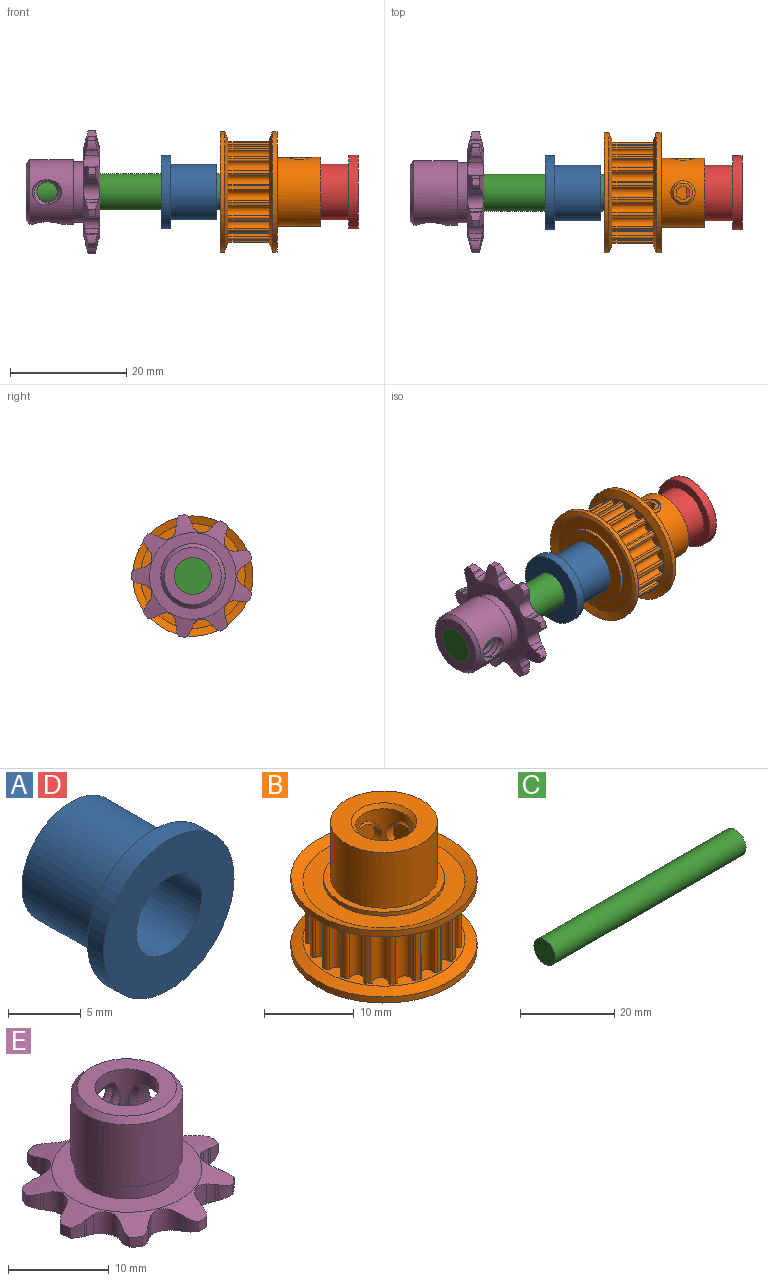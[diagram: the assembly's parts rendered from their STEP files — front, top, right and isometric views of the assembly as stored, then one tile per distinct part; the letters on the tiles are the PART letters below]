
ASSEMBLY  parts=5 mates=4
PART A: 6 faces, bbox 12.7x9.5x12.7 mm
  f0: cylinder r=6.35mm len=12.7mm, axis (0,-1,0), area 63.3mm2, adj f4,f5
  f1: cylinder r=3.19mm len=9.53mm, axis (0,-1,0), area 190.8mm2, adj f3,f4
  f2: cylinder r=4.79mm len=9.58mm, axis (0,-1,0), area 238.8mm2, adj f3,f5
  f3: plane 9.58x9.58mm, normal (0,1,0), area 40.1mm2, adj f1,f2
  f4: plane 12.7x12.7mm, normal (0,-1,0), area 94.8mm2, adj f0,f1
  f5: plane 12.7x12.7mm, normal (0,1,0), area 54.7mm2, adj f0,f2
PART B: 121 faces, bbox 20.7x20.7x17.3 mm
  f0: plane 11.89x11.89mm, normal (0,0,1), area 69.1mm2, adj f1,f6
  f1: cone r=3.41mm half-angle=45deg, axis (0,0,1), area 14.4mm2, adj f0,f2
  f2: cylinder r=3.17mm len=16.39mm, axis (0,0,-1), area 298mm2, adj f1,f4,f31,f99
  f3: cylinder r=2.08mm len=4.17mm, axis (0,-1,0), area 3mm2, adj f5,f6
  f4: cylinder r=2.08mm len=4.17mm, axis (0,-1,0), area 10.4mm2, adj f2,f119
  f5: cone r=1.87mm half-angle=45deg, axis (0,-1,0), area 6.9mm2, adj f3,f111
  f6: cylinder r=5.94mm len=11.89mm, axis (0,0,-1), area 253.9mm2, adj f0,f3,f7,f98
  f7: plane 13.46x13.46mm, normal (0,0,1), area 31.4mm2, adj f6,f8
  f8: cylinder r=6.73mm len=13.46mm, axis (0,0,-1), area 22.6mm2, adj f7,f9
  f9: plane 18.03x18.03mm, normal (0,0,1), area 113.1mm2, adj f8,f10
  f10: cone r=9.68mm half-angle=68.2deg, axis (0,0,1), area 87.4mm2, adj f9,f11
  f11: cylinder r=10.35mm len=20.7mm, axis (0,0,-1), area 52.9mm2, adj f10,f12
  f12: cone r=9.68mm half-angle=68.2deg, axis (0,0,1), area 87.4mm2, adj f11,f13
  f13: plane 18.03x18.03mm, normal (0,0,-1), area 55.8mm2, adj f12,f14,f15,f16,f17,f18,f19,f20
  f14: cylinder r=8.69mm len=7.11mm, axis (0,0,-1), area 4.1mm2, adj f13,f24,f32,f97
  f15: cylinder r=8.69mm len=7.11mm, axis (0,0,-1), area 4.1mm2, adj f13,f24,f94,f95
  f16: cylinder r=8.69mm len=7.11mm, axis (0,0,-1), area 4.1mm2, adj f13,f24,f91,f92
  f17: cylinder r=8.69mm len=7.11mm, axis (0,0,-1), area 4.1mm2, adj f13,f24,f88,f89
  f18: cylinder r=8.69mm len=7.11mm, axis (0,0,-1), area 4.1mm2, adj f13,f24,f85,f86
  f19: cylinder r=8.69mm len=7.11mm, axis (0,0,-1), area 4.1mm2, adj f13,f24,f82,f83
  f20: cylinder r=8.69mm len=7.11mm, axis (0,0,-1), area 4.1mm2, adj f13,f24,f79,f80
  f21: cylinder r=8.69mm len=7.11mm, axis (0,0,-1), area 4.1mm2, adj f13,f24,f76,f77
  f22: cylinder r=8.69mm len=7.11mm, axis (0,0,-1), area 4.1mm2, adj f13,f24,f73,f74
  f23: cylinder r=8.69mm len=7.11mm, axis (0,0,-1), area 4.1mm2, adj f13,f24,f49,f71
  f24: plane 18.03x18.03mm, normal (0,0,1), area 55.8mm2, adj f14,f15,f16,f17,f18,f19,f20,f21
  f25: cone r=9.68mm half-angle=68.2deg, axis (0,0,-1), area 87.4mm2, adj f24,f26
  f26: cylinder r=10.35mm len=20.7mm, axis (0,0,-1), area 52.9mm2, adj f25,f27
  f27: cone r=9.68mm half-angle=68.2deg, axis (0,0,-1), area 87.4mm2, adj f26,f28
  f28: plane 18.03x18.03mm, normal (0,0,-1), area 113.1mm2, adj f27,f29
  f29: cylinder r=6.73mm len=13.46mm, axis (0,0,-1), area 22.6mm2, adj f28,f30
  f30: plane 13.46x13.46mm, normal (0,0,-1), area 100.5mm2, adj f29,f31
  f31: cone r=3.41mm half-angle=45deg, axis (0,0,-1), area 14.4mm2, adj f2,f30
  f32: cylinder r=0.25mm len=7.11mm, axis (0,0,1), area 3.3mm2, adj f13,f14,f24,f33
  f33: cylinder r=0.86mm len=7.11mm, axis (0,0,1), area 20.7mm2, adj f13,f24,f32,f34
  f34: cylinder r=0.25mm len=7.11mm, axis (0,0,1), area 3.3mm2, adj f13,f24,f33,f43
  f35: cylinder r=8.69mm len=7.11mm, axis (0,0,-1), area 4.1mm2, adj f13,f24,f44,f47
  f36: cylinder r=8.69mm len=7.11mm, axis (0,0,-1), area 4.1mm2, adj f13,f24,f46,f50
  f37: cylinder r=8.69mm len=7.11mm, axis (0,0,-1), area 4.1mm2, adj f13,f24,f52,f53
  f38: cylinder r=8.69mm len=7.11mm, axis (0,0,-1), area 4.1mm2, adj f13,f24,f55,f56
  f39: cylinder r=8.69mm len=7.11mm, axis (0,0,-1), area 4.1mm2, adj f13,f24,f58,f59
  f40: cylinder r=8.69mm len=7.11mm, axis (0,0,-1), area 4.1mm2, adj f13,f24,f61,f62
  f41: cylinder r=8.69mm len=7.11mm, axis (0,0,-1), area 4.1mm2, adj f13,f24,f64,f65
  f42: cylinder r=8.69mm len=7.11mm, axis (0,0,-1), area 4.1mm2, adj f13,f24,f67,f68
  f43: cylinder r=8.69mm len=7.11mm, axis (0,0,-1), area 4.1mm2, adj f13,f24,f34,f70
  f44: cylinder r=0.25mm len=7.11mm, axis (0,0,1), area 3.3mm2, adj f13,f24,f35,f45
  f45: cylinder r=0.86mm len=7.11mm, axis (0,0,1), area 20.7mm2, adj f13,f24,f44,f46
  f46: cylinder r=0.25mm len=7.11mm, axis (0,0,1), area 3.3mm2, adj f13,f24,f36,f45
  f47: cylinder r=0.25mm len=7.11mm, axis (0,0,1), area 3.3mm2, adj f13,f24,f35,f48
  f48: cylinder r=0.86mm len=7.11mm, axis (0,0,1), area 20.7mm2, adj f13,f24,f47,f49
  f49: cylinder r=0.25mm len=7.11mm, axis (0,0,1), area 3.3mm2, adj f13,f23,f24,f48
  f50: cylinder r=0.25mm len=7.11mm, axis (0,0,1), area 3.3mm2, adj f13,f24,f36,f51
  f51: cylinder r=0.86mm len=7.11mm, axis (0,0,1), area 20.7mm2, adj f13,f24,f50,f52
  f52: cylinder r=0.25mm len=7.11mm, axis (0,0,1), area 3.3mm2, adj f13,f24,f37,f51
  f53: cylinder r=0.25mm len=7.11mm, axis (0,0,1), area 3.3mm2, adj f13,f24,f37,f54
  f54: cylinder r=0.86mm len=7.11mm, axis (0,0,1), area 20.7mm2, adj f13,f24,f53,f55
  f55: cylinder r=0.25mm len=7.11mm, axis (0,0,1), area 3.3mm2, adj f13,f24,f38,f54
  f56: cylinder r=0.25mm len=7.11mm, axis (0,0,1), area 3.3mm2, adj f13,f24,f38,f57
  f57: cylinder r=0.86mm len=7.11mm, axis (0,0,1), area 20.7mm2, adj f13,f24,f56,f58
  f58: cylinder r=0.25mm len=7.11mm, axis (0,0,1), area 3.3mm2, adj f13,f24,f39,f57
  f59: cylinder r=0.25mm len=7.11mm, axis (0,0,1), area 3.3mm2, adj f13,f24,f39,f60
  f60: cylinder r=0.86mm len=7.11mm, axis (0,0,1), area 20.7mm2, adj f13,f24,f59,f61
  f61: cylinder r=0.25mm len=7.11mm, axis (0,0,1), area 3.3mm2, adj f13,f24,f40,f60
  f62: cylinder r=0.25mm len=7.11mm, axis (0,0,1), area 3.3mm2, adj f13,f24,f40,f63
  f63: cylinder r=0.86mm len=7.11mm, axis (0,0,1), area 20.7mm2, adj f13,f24,f62,f64
  f64: cylinder r=0.25mm len=7.11mm, axis (0,0,1), area 3.3mm2, adj f13,f24,f41,f63
  f65: cylinder r=0.25mm len=7.11mm, axis (0,0,1), area 3.3mm2, adj f13,f24,f41,f66
  f66: cylinder r=0.86mm len=7.11mm, axis (0,0,1), area 20.7mm2, adj f13,f24,f65,f67
  f67: cylinder r=0.25mm len=7.11mm, axis (0,0,1), area 3.3mm2, adj f13,f24,f42,f66
  f68: cylinder r=0.25mm len=7.11mm, axis (0,0,1), area 3.3mm2, adj f13,f24,f42,f69
  f69: cylinder r=0.86mm len=7.11mm, axis (0,0,1), area 20.7mm2, adj f13,f24,f68,f70
  f70: cylinder r=0.25mm len=7.11mm, axis (0,0,1), area 3.3mm2, adj f13,f24,f43,f69
  f71: cylinder r=0.25mm len=7.11mm, axis (0,0,1), area 3.3mm2, adj f13,f23,f24,f72
  f72: cylinder r=0.86mm len=7.11mm, axis (0,0,1), area 20.7mm2, adj f13,f24,f71,f73
  f73: cylinder r=0.25mm len=7.11mm, axis (0,0,1), area 3.3mm2, adj f13,f22,f24,f72
  f74: cylinder r=0.25mm len=7.11mm, axis (0,0,1), area 3.3mm2, adj f13,f22,f24,f75
  f75: cylinder r=0.86mm len=7.11mm, axis (0,0,1), area 20.7mm2, adj f13,f24,f74,f76
  f76: cylinder r=0.25mm len=7.11mm, axis (0,0,1), area 3.3mm2, adj f13,f21,f24,f75
  f77: cylinder r=0.25mm len=7.11mm, axis (0,0,1), area 3.3mm2, adj f13,f21,f24,f78
  f78: cylinder r=0.86mm len=7.11mm, axis (0,0,1), area 20.7mm2, adj f13,f24,f77,f79
  f79: cylinder r=0.25mm len=7.11mm, axis (0,0,1), area 3.3mm2, adj f13,f20,f24,f78
  f80: cylinder r=0.25mm len=7.11mm, axis (0,0,1), area 3.3mm2, adj f13,f20,f24,f81
  f81: cylinder r=0.86mm len=7.11mm, axis (0,0,1), area 20.7mm2, adj f13,f24,f80,f82
  f82: cylinder r=0.25mm len=7.11mm, axis (0,0,1), area 3.3mm2, adj f13,f19,f24,f81
  f83: cylinder r=0.25mm len=7.11mm, axis (0,0,1), area 3.3mm2, adj f13,f19,f24,f84
  f84: cylinder r=0.86mm len=7.11mm, axis (0,0,1), area 20.7mm2, adj f13,f24,f83,f85
  f85: cylinder r=0.25mm len=7.11mm, axis (0,0,1), area 3.3mm2, adj f13,f18,f24,f84
  f86: cylinder r=0.25mm len=7.11mm, axis (0,0,1), area 3.3mm2, adj f13,f18,f24,f87
  f87: cylinder r=0.86mm len=7.11mm, axis (0,0,1), area 20.7mm2, adj f13,f24,f86,f88
  f88: cylinder r=0.25mm len=7.11mm, axis (0,0,1), area 3.3mm2, adj f13,f17,f24,f87
  f89: cylinder r=0.25mm len=7.11mm, axis (0,0,1), area 3.3mm2, adj f13,f17,f24,f90
  f90: cylinder r=0.86mm len=7.11mm, axis (0,0,1), area 20.7mm2, adj f13,f24,f89,f91
  f91: cylinder r=0.25mm len=7.11mm, axis (0,0,1), area 3.3mm2, adj f13,f16,f24,f90
  f92: cylinder r=0.25mm len=7.11mm, axis (0,0,1), area 3.3mm2, adj f13,f16,f24,f93
  f93: cylinder r=0.86mm len=7.11mm, axis (0,0,1), area 20.7mm2, adj f13,f24,f92,f94
  f94: cylinder r=0.25mm len=7.11mm, axis (0,0,1), area 3.3mm2, adj f13,f15,f24,f93
  f95: cylinder r=0.25mm len=7.11mm, axis (0,0,1), area 3.3mm2, adj f13,f15,f24,f96
  f96: cylinder r=0.86mm len=7.11mm, axis (0,0,1), area 20.7mm2, adj f13,f24,f95,f97
  f97: cylinder r=0.25mm len=7.11mm, axis (0,0,1), area 3.3mm2, adj f13,f14,f24,f96
  f98: cylinder r=2.08mm len=4.17mm, axis (-1,0,0), area 3mm2, adj f6,f100
  f99: cylinder r=2.08mm len=4.17mm, axis (-1,0,0), area 10.4mm2, adj f2,f101
  f100: cone r=1.87mm half-angle=45deg, axis (-1,0,0), area 6.9mm2, adj f98,f103
  f101: cone r=1.87mm half-angle=45deg, axis (1,0,0), area 6.9mm2, adj f99,f102
  f102: plane 3.33x3.33mm, normal (-1,0,0), area 8.7mm2, adj f101
  f103: plane 3.33x3.33mm, normal (1,0,0), area 5mm2, adj f100,f104,f105,f106,f107,f108,f109
  f104: plane 2.08x1.04mm, normal (0,-0.87,0.5), area 2.5mm2, adj f103,f105,f109,f110
  f105: plane 2.08x1.2mm, normal (0,0,1), area 2.5mm2, adj f103,f104,f106,f110
  f106: plane 2.08x1.04mm, normal (0,0.87,0.5), area 2.5mm2, adj f103,f105,f107,f110
  f107: plane 2.08x1.04mm, normal (0,0.87,-0.5), area 2.5mm2, adj f103,f106,f108,f110
  f108: plane 2.08x1.2mm, normal (0,0,-1), area 2.5mm2, adj f103,f107,f109,f110
  f109: plane 2.08x1.04mm, normal (0,-0.87,-0.5), area 2.5mm2, adj f103,f104,f108,f110
  f110: plane 2.41x2.08mm, normal (1,0,0), area 3.8mm2, adj f104,f105,f106,f107,f108,f109
  f111: plane 3.33x3.33mm, normal (0,1,0), area 5mm2, adj f5,f112,f113,f114,f115,f116,f117
  f112: plane 2.08x1.04mm, normal (0.87,0,0.5), area 2.5mm2, adj f111,f113,f117,f118
  f113: plane 2.08x1.2mm, normal (0,0,1), area 2.5mm2, adj f111,f112,f114,f118
  f114: plane 2.08x1.04mm, normal (-0.87,0,0.5), area 2.5mm2, adj f111,f113,f115,f118
  f115: plane 2.08x1.04mm, normal (-0.87,0,-0.5), area 2.5mm2, adj f111,f114,f116,f118
  f116: plane 2.08x1.2mm, normal (0,0,-1), area 2.5mm2, adj f111,f115,f117,f118
  f117: plane 2.08x1.04mm, normal (0.87,0,-0.5), area 2.5mm2, adj f111,f112,f116,f118
  f118: plane 2.41x2.08mm, normal (0,1,0), area 3.8mm2, adj f112,f113,f114,f115,f116,f117
  f119: cone r=1.87mm half-angle=45deg, axis (0,1,0), area 6.9mm2, adj f4,f120
  f120: plane 3.33x3.33mm, normal (0,-1,0), area 8.7mm2, adj f119
PART C: 3 faces, bbox 57.2x6.4x6.4 mm
  f0: cylinder r=3.17mm len=57.15mm, axis (-1,0,0), area 1140.1mm2, adj f1,f2
  f1: plane 6.35x6.35mm, normal (1,0,0), area 31.7mm2, adj f0
  f2: plane 6.35x6.35mm, normal (-1,0,0), area 31.7mm2, adj f0
PART D: same geometry as A
PART E: 104 faces, bbox 21.3x21.3x12.7 mm
  f0: cone r=2.53mm half-angle=45deg, axis (1,0,0), area 5.2mm2, adj f1,f100,f101,f102,f103
  f1: cylinder r=1.75mm len=3.5mm, axis (1,0,0), area 3mm2, adj f0,f2,f100,f103
  f2: cylinder r=3.17mm len=12.7mm, axis (0,0,-1), area 224.8mm2, adj f1,f3,f4,f7,f8,f9,f10,f11
  f3: cylinder r=1.75mm len=1.44mm, axis (0,1,0), area 0mm2, adj f2,f11
  f4: cylinder r=1.75mm len=3.5mm, axis (0,1,0), area 3mm2, adj f2,f5,f9,f11
  f5: cone r=2.53mm half-angle=45deg, axis (0,1,0), area 5.2mm2, adj f4,f6,f9,f11,f102
  f6: cylinder r=2.41mm len=0.66mm, axis (0,1,0), area 0mm2, adj f5,f11,f102
  f7: bspline ~3.65x1.27mm, area 0mm2, adj f2,f8
  f8: cylinder r=2.41mm len=3.57mm, axis (0,1,0), area 0.5mm2, adj f2,f7,f9
  f9: bspline ~4.83x4.83mm, area 21.5mm2, adj f2,f4,f5,f8,f10,f102
  f10: cylinder r=2.41mm len=4.83mm, axis (0,1,0), area 4.2mm2, adj f2,f9,f11,f102
  f11: bspline ~4.82x4.82mm, area 21.8mm2, adj f2,f3,f4,f5,f6,f10,f102
  f12: cylinder r=2.41mm len=1.46mm, axis (1,0,0), area 0mm2, adj f2,f13
  f13: bspline ~1.77x0.52mm, area 0mm2, adj f2,f12
  f14: bspline ~1.77x0.52mm, area 0mm2, adj f2,f15
  f15: cylinder r=2.41mm len=1.46mm, axis (0,1,0), area 0.1mm2, adj f2,f14,f16
  f16: bspline ~3.65x1.26mm, area 0.7mm2, adj f2,f15,f17
  f17: cylinder r=2.41mm len=3.57mm, axis (1,0,0), area 0.5mm2, adj f2,f16,f103
  f18: plane 9.84x9.84mm, normal (0,0,1), area 44.4mm2, adj f2,f19
  f19: cone r=4.92mm half-angle=45deg, axis (0,0,-1), area 29.6mm2, adj f18,f102
  f20: cylinder r=2.41mm len=4.83mm, axis (1,0,0), area 4.2mm2, adj f2,f100,f102,f103
  f21: cylinder r=1.75mm len=1.44mm, axis (1,0,0), area 0mm2, adj f2,f100
  f22: plane 14.91x14.91mm, normal (0,0,-1), area 142.8mm2, adj f2,f23
  f23: cone r=7.45mm half-angle=76deg, axis (0,0,1), area 84mm2, adj f22,f24,f29,f30,f31,f32,f33,f34
  f24: cylinder r=1.7mm len=2.5mm, axis (0,0,1), area 6.9mm2, adj f23,f25,f29,f99
  f25: cone r=10.63mm half-angle=76deg, axis (0,0,-1), area 84mm2, adj f24,f26,f29,f30,f31,f32,f33,f34
  f26: plane 14.91x14.91mm, normal (0,0,1), area 90.6mm2, adj f25,f27
  f27: cylinder r=5.17mm len=10.33mm, axis (0,0,-1), area 56.7mm2, adj f26,f28
  f28: plane 11.11x11.11mm, normal (0,0,-1), area 13.1mm2, adj f27,f102
  f29: cylinder r=4.34mm len=2.39mm, axis (0,0,1), area 2mm2, adj f23,f24,f25,f30
  f30: plane 1.99x0.2mm, normal (0.64,-0.77,0), area 0.5mm2, adj f23,f25,f29,f31
  f31: cylinder r=2.8mm len=1.87mm, axis (0,0,1), area 2.4mm2, adj f23,f25,f30,f32
  f32: cylinder r=10.63mm len=1.21mm, axis (0,0,-1), area 1.5mm2, adj f23,f25,f31,f33
  f33: cylinder r=2.8mm len=1.87mm, axis (0,0,1), area 2.4mm2, adj f23,f25,f32,f34
  f34: plane 1.99x0.24mm, normal (-0.34,0.94,0), area 0.5mm2, adj f23,f25,f33,f35
  f35: cylinder r=4.34mm len=2.39mm, axis (0,0,1), area 2mm2, adj f23,f25,f34,f36
  f36: cylinder r=1.7mm len=2.39mm, axis (0,0,1), area 6.9mm2, adj f23,f25,f35,f37
  f37: cylinder r=4.34mm len=2.39mm, axis (0,0,1), area 2mm2, adj f23,f25,f36,f38
  f38: plane 1.99x0.25mm, normal (0.98,-0.18,0), area 0.5mm2, adj f23,f25,f37,f39
  f39: cylinder r=2.8mm len=1.87mm, axis (0,0,1), area 2.4mm2, adj f23,f25,f38,f40
  f40: cylinder r=10.63mm len=1.21mm, axis (0,0,-1), area 1.5mm2, adj f23,f25,f39,f41
  f41: cylinder r=2.8mm len=1.87mm, axis (0,0,1), area 2.4mm2, adj f23,f25,f40,f42
  f42: plane 1.99x0.22mm, normal (-0.87,0.5,0), area 0.5mm2, adj f23,f25,f41,f43
  f43: cylinder r=4.34mm len=2.39mm, axis (0,0,1), area 2mm2, adj f23,f25,f42,f44
  f44: cylinder r=1.7mm len=2.54mm, axis (0,0,1), area 6.9mm2, adj f23,f25,f43,f45
  f45: cylinder r=4.34mm len=2.39mm, axis (0,0,1), area 2mm2, adj f23,f25,f44,f46
  f46: plane 1.99x0.22mm, normal (0.87,0.5,0), area 0.5mm2, adj f23,f25,f45,f47
  f47: cylinder r=2.8mm len=1.87mm, axis (0,0,1), area 2.4mm2, adj f23,f25,f46,f48
  f48: cylinder r=10.63mm len=1.21mm, axis (0,0,-1), area 1.5mm2, adj f23,f25,f47,f49
  f49: cylinder r=2.8mm len=1.87mm, axis (0,0,1), area 2.4mm2, adj f23,f25,f48,f50
  f50: plane 1.99x0.25mm, normal (-0.98,-0.18,0), area 0.5mm2, adj f23,f25,f49,f51
  f51: cylinder r=4.34mm len=2.39mm, axis (0,0,1), area 2mm2, adj f23,f25,f50,f52
  f52: cylinder r=1.7mm len=2.39mm, axis (0,0,1), area 6.9mm2, adj f23,f25,f51,f53
  f53: cylinder r=4.34mm len=2.39mm, axis (0,0,1), area 2mm2, adj f23,f25,f52,f54
  f54: plane 1.99x0.24mm, normal (0.34,0.94,0), area 0.5mm2, adj f23,f25,f53,f55
  f55: cylinder r=2.8mm len=1.87mm, axis (0,0,1), area 2.4mm2, adj f23,f25,f54,f56
  f56: cylinder r=10.63mm len=1.21mm, axis (0,0,-1), area 1.5mm2, adj f23,f25,f55,f57
  f57: cylinder r=2.8mm len=1.87mm, axis (0,0,1), area 2.4mm2, adj f23,f25,f56,f58
  f58: plane 1.99x0.2mm, normal (-0.64,-0.77,0), area 0.5mm2, adj f23,f25,f57,f59
  f59: cylinder r=4.34mm len=2.39mm, axis (0,0,1), area 2mm2, adj f23,f25,f58,f60
  f60: cylinder r=1.7mm len=2.71mm, axis (0,0,1), area 7.3mm2, adj f23,f25,f59,f61
  f61: cylinder r=4.34mm len=2.39mm, axis (0,0,1), area 2mm2, adj f23,f25,f60,f62
  f62: plane 1.99x0.24mm, normal (-0.34,0.94,0), area 0.5mm2, adj f23,f25,f61,f63
  f63: cylinder r=2.8mm len=1.87mm, axis (0,0,1), area 2.4mm2, adj f23,f25,f62,f64
  f64: cylinder r=10.63mm len=1.23mm, axis (0,0,-1), area 1.5mm2, adj f23,f25,f63,f65
  f65: cylinder r=2.8mm len=1.87mm, axis (0,0,1), area 2.4mm2, adj f23,f25,f64,f66
  f66: plane 1.99x0.26mm, normal (0,-1,0), area 0.5mm2, adj f23,f25,f65,f67
  f67: cylinder r=4.34mm len=2.39mm, axis (0,0,1), area 2mm2, adj f23,f25,f66,f68
  f68: cylinder r=1.7mm len=2.59mm, axis (0,0,1), area 7.1mm2, adj f23,f25,f67,f69
  f69: cylinder r=4.34mm len=2.39mm, axis (0,0,1), area 2mm2, adj f23,f25,f68,f70
  f70: plane 1.99x0.22mm, normal (-0.87,0.5,0), area 0.5mm2, adj f23,f25,f69,f71
  f71: cylinder r=2.8mm len=1.87mm, axis (0,0,1), area 2.4mm2, adj f23,f25,f70,f72
  f72: cylinder r=10.63mm len=1.21mm, axis (0,0,-1), area 1.5mm2, adj f23,f25,f71,f73
  f73: cylinder r=2.8mm len=1.87mm, axis (0,0,1), area 2.4mm2, adj f23,f25,f72,f74
  f74: plane 1.99x0.2mm, normal (0.64,-0.76,0), area 0.5mm2, adj f23,f25,f73,f75
  f75: cylinder r=4.34mm len=2.39mm, axis (0,0,1), area 2mm2, adj f23,f25,f74,f76
  f76: cylinder r=1.7mm len=2.39mm, axis (0,0,1), area 6.9mm2, adj f23,f25,f75,f77
  f77: cylinder r=4.34mm len=2.39mm, axis (0,0,1), area 2mm2, adj f23,f25,f76,f78
  f78: plane 1.99x0.25mm, normal (-0.99,-0.17,0), area 0.5mm2, adj f23,f25,f77,f79
  f79: cylinder r=2.8mm len=1.87mm, axis (0,0,1), area 2.4mm2, adj f23,f25,f78,f80
  f80: cylinder r=10.63mm len=1.25mm, axis (0,0,-1), area 1.5mm2, adj f23,f25,f79,f81
  f81: cylinder r=2.8mm len=1.87mm, axis (0,0,1), area 2.4mm2, adj f23,f25,f80,f82
  f82: plane 1.99x0.25mm, normal (0.99,-0.17,0), area 0.5mm2, adj f23,f25,f81,f83
  f83: cylinder r=4.34mm len=2.39mm, axis (0,0,1), area 2mm2, adj f23,f25,f82,f84
  f84: cylinder r=1.7mm len=2.39mm, axis (0,0,1), area 6.9mm2, adj f23,f25,f83,f85
  f85: cylinder r=4.34mm len=2.39mm, axis (0,0,1), area 2mm2, adj f23,f25,f84,f86
  f86: plane 1.99x0.2mm, normal (-0.64,-0.76,0), area 0.5mm2, adj f23,f25,f85,f87
  f87: cylinder r=2.8mm len=1.87mm, axis (0,0,1), area 2.4mm2, adj f23,f25,f86,f88
  f88: cylinder r=10.63mm len=1.21mm, axis (0,0,-1), area 1.5mm2, adj f23,f25,f87,f89
  f89: cylinder r=2.8mm len=1.87mm, axis (0,0,1), area 2.4mm2, adj f23,f25,f88,f90
  f90: plane 1.99x0.22mm, normal (0.87,0.5,0), area 0.5mm2, adj f23,f25,f89,f91
  f91: cylinder r=4.34mm len=2.39mm, axis (0,0,1), area 2mm2, adj f23,f25,f90,f92
  f92: cylinder r=1.7mm len=2.39mm, axis (0,0,1), area 6.9mm2, adj f23,f25,f91,f93
  f93: cylinder r=4.34mm len=2.39mm, axis (0,0,1), area 2mm2, adj f23,f25,f92,f94
  f94: plane 1.99x0.26mm, normal (0,-1,0), area 0.5mm2, adj f23,f25,f93,f95
  f95: cylinder r=2.8mm len=1.87mm, axis (0,0,1), area 2.4mm2, adj f23,f25,f94,f96
  f96: cylinder r=10.63mm len=1.23mm, axis (0,0,-1), area 1.5mm2, adj f23,f25,f95,f97
  f97: cylinder r=2.8mm len=1.87mm, axis (0,0,1), area 2.4mm2, adj f23,f25,f96,f98
  f98: plane 1.99x0.24mm, normal (0.34,0.94,0), area 0.5mm2, adj f23,f25,f97,f99
  f99: cylinder r=4.34mm len=2.39mm, axis (0,0,1), area 2mm2, adj f23,f24,f25,f98
  f100: bspline ~4.82x4.82mm, area 21.9mm2, adj f0,f1,f2,f20,f21,f101,f102
  f101: cylinder r=2.41mm len=0.66mm, axis (1,0,0), area 0mm2, adj f0,f100,f102
  f102: cylinder r=5.56mm len=11.11mm, axis (0,0,-1), area 227.9mm2, adj f0,f5,f6,f9,f10,f11,f19,f20
  f103: bspline ~4.83x4.83mm, area 21.6mm2, adj f0,f1,f2,f17,f20,f102
PLACE A rot(axis=(-0.58,-0.58,-0.58),120deg) t=(98.58,138.17,34.25)mm
PLACE B rot(axis=(0.58,0.58,0.58),120deg) t=(118.49,138.17,34.25)mm
PLACE C rot(axis=(0,1,0),180deg) t=(157.82,-50.53,49.28)mm
PLACE D rot(axis=(0,0,1),90deg) t=(132.42,138.17,34.25)mm
PLACE E rot(axis=(0.71,0,-0.71),180deg) t=(86.57,138.17,34.25)mm
MATE slider B.f1 <-> C.f0  axis (1,0,0) through (126.04,138.17,34.25)mm
MATE fastened C.f0 <-> E.f27  axis (1,0,0) through (75.27,138.17,34.25)mm
MATE slider C.f0 <-> D.f0  axis (1,0,0) through (132.42,138.17,34.25)mm
MATE slider A.f0 <-> C.f0  axis (-1,0,0) through (98.58,138.17,34.25)mm
